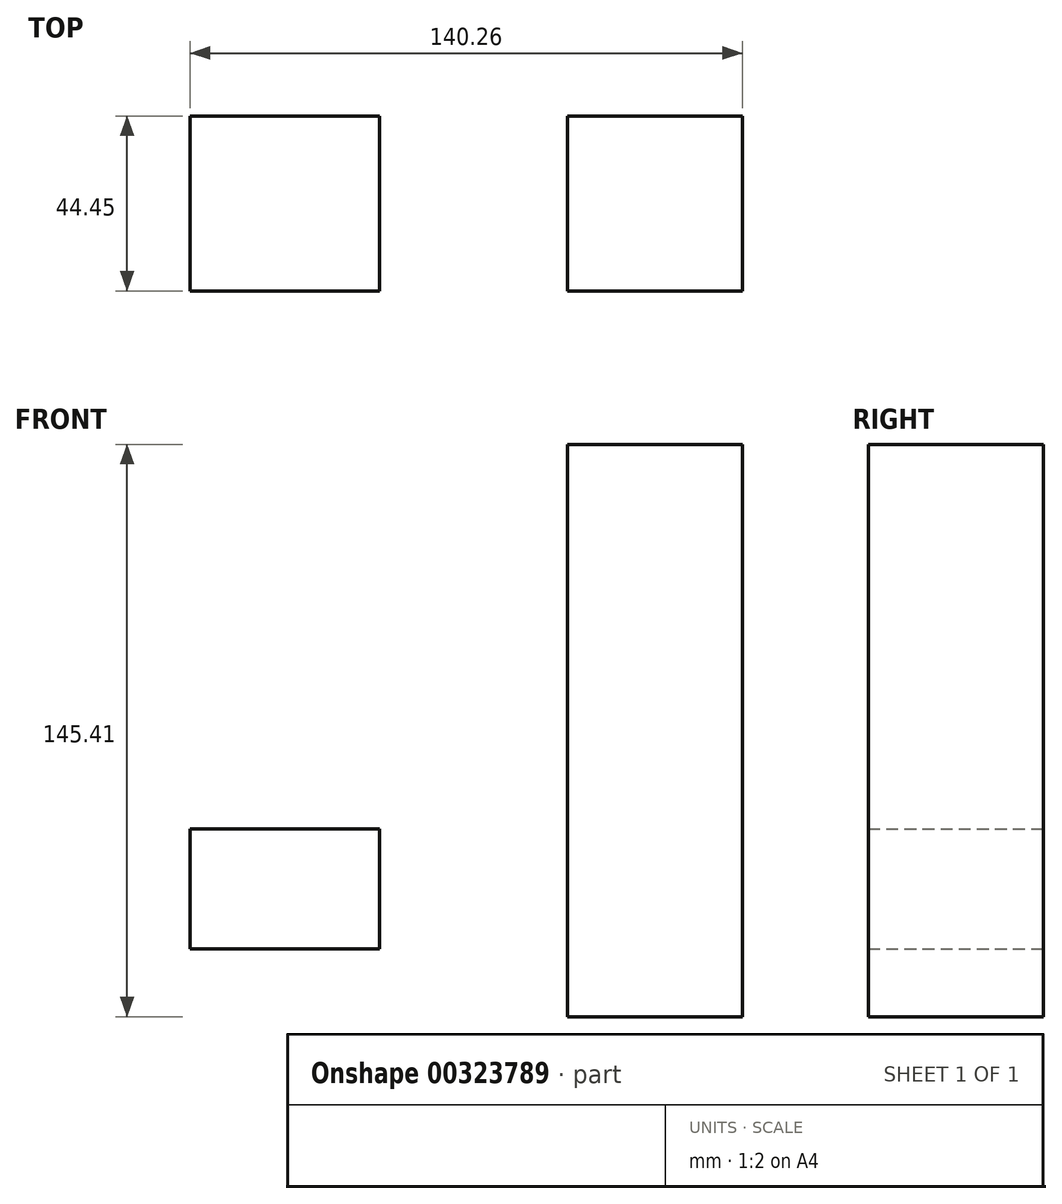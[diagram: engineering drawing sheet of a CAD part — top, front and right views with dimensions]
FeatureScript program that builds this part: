
annotation { "Feature Type Name" : "Feature", "Feature Type Description" : "" }
export const myFeature = defineFeature(function(context is Context, id is Id, definition is map)
    precondition{}
    {
        {
            var Q0;
            Q0=qCreatedBy(makeId("Front.planeOp"),FACE);
            var sketch = newSketch(context, id + "F0", { "sketchPlane" : qUnion([Q0])});
            skLineSegment(sketch, "E0.bottom", {"start": v(-44.65, 5.2) * mm, "end": v(-89.1, 5.2) * mm});
            skLineSegment(sketch, "E0.top", {"start": v(-44.65, 150.61) * mm, "end": v(-89.1, 150.61) * mm});
            skLineSegment(sketch, "E0.left", {"start": v(-44.65, 5.2) * mm, "end": v(-44.65, 150.61) * mm});
            skLineSegment(sketch, "E0.right", {"start": v(-89.1, 5.2) * mm, "end": v(-89.1, 150.61) * mm});
            skPoint(sketch, "E0.middle", {"position": v(-66.88, 77.9) * mm});
            skSolve(sketch);
        }
        {
            var Q0;
            Q0=makeQuery(id+"F0.imprint","IMPRINT",FACE,{"disambiguationData":[TD([[makeQuery(id+"F0.imprint","IMPRINT",EDGE,{"derivedFrom":sQuery(id+"F0.wireOp",EDGE,"E0.bottom")}),-1.0]])]});
            var sketch = newSketch(context, id + "F1", { "sketchPlane" : qUnion([Q0])});
            skLineSegment(sketch, "E1.bottom", {"start": v(-136.78, 22.4) * mm, "end": v(-184.9, 22.4) * mm});
            skLineSegment(sketch, "E1.top", {"start": v(-136.78, 52.87) * mm, "end": v(-184.9, 52.87) * mm});
            skLineSegment(sketch, "E1.left", {"start": v(-136.78, 22.4) * mm, "end": v(-136.78, 52.87) * mm});
            skLineSegment(sketch, "E1.right", {"start": v(-184.9, 22.4) * mm, "end": v(-184.9, 52.87) * mm});
            skPoint(sketch, "E1.middle", {"position": v(-160.85, 37.63) * mm});
            skSolve(sketch);
        }
        {
            var Q0;
            Q0=makeQuery(id+"F0.imprint","IMPRINT",FACE,{"disambiguationData":[TD([[makeQuery(id+"F0.imprint","IMPRINT",EDGE,{"derivedFrom":sQuery(id+"F0.wireOp",EDGE,"E0.bottom")}),-1.0]])]});
            var Q1;
            Q1=makeQuery(id+"F1.imprint","IMPRINT",FACE,{"disambiguationData":[TD([[makeQuery(id+"F1.imprint","IMPRINT",EDGE,{"derivedFrom":sQuery(id+"F1.wireOp",EDGE,"E1.bottom")}),-1.0]])]});
            extrude(context, id + "F2", {"entities" : qUnion([Q0, Q1]), "depth" : 44.45 * mm});
        }
    });
